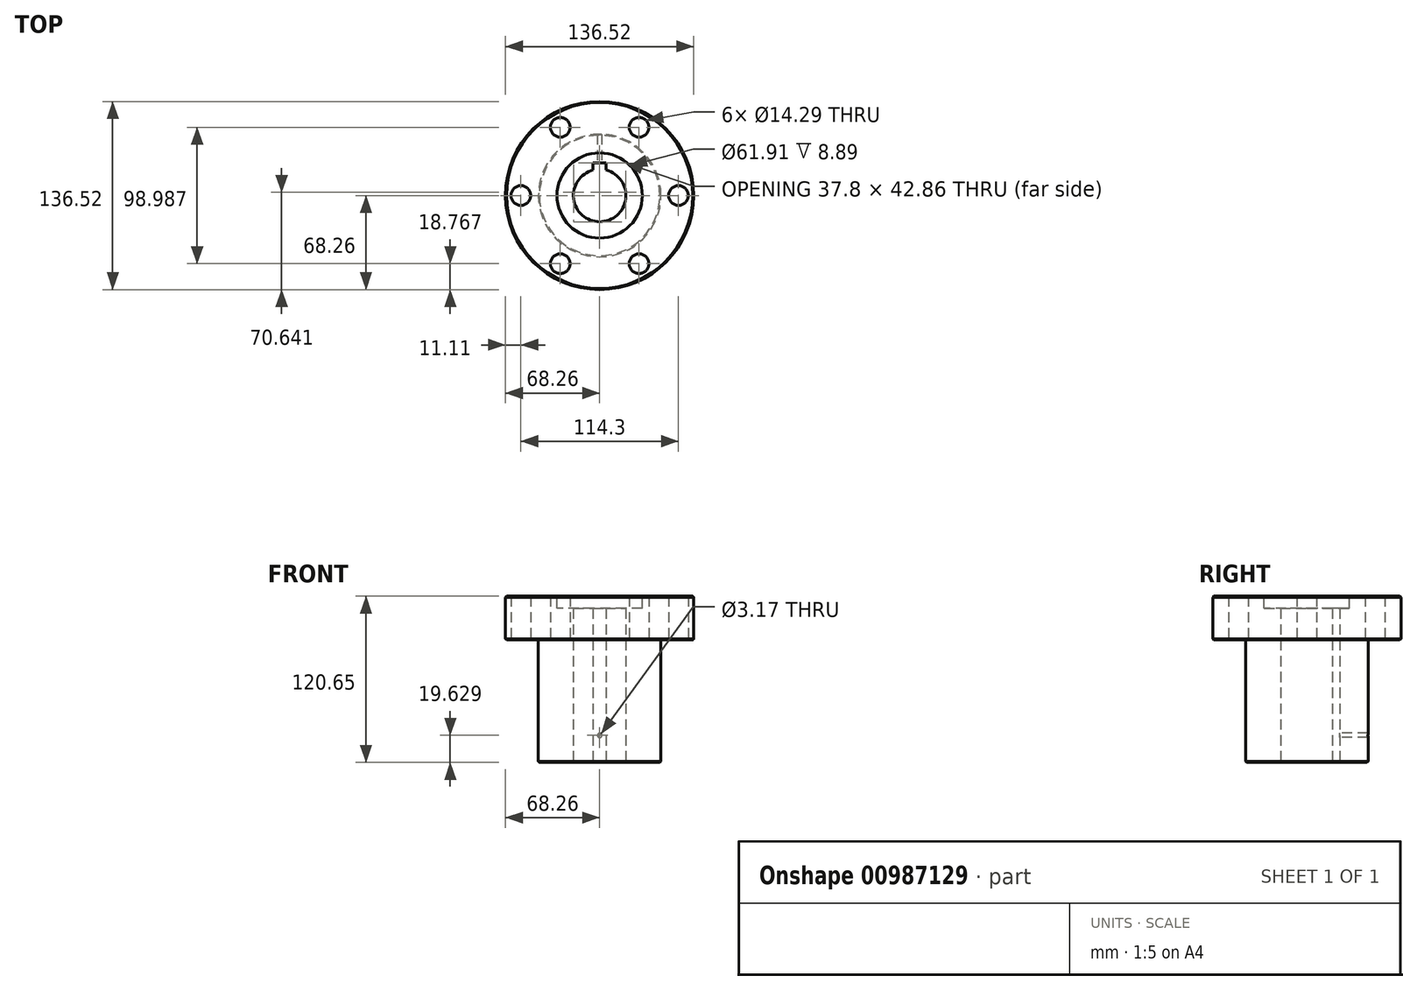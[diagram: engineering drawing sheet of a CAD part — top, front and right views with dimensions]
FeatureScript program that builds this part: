
annotation { "Feature Type Name" : "Feature", "Feature Type Description" : "" }
export const myFeature = defineFeature(function(context is Context, id is Id, definition is map)
    precondition{}
    {
        {
            var Q0;
            Q0=qCreatedBy(makeId("Top.planeOp"),FACE);
            var sketch = newSketch(context, id + "F0", { "sketchPlane" : qUnion([Q0])});
            skCircle(sketch, "E0", {"center": v(0, 0) * mm, "radius": 68.26 * mm});
            skCircle(sketch, "E1", {"center": v(0, 0) * mm, "radius": 19.05 * mm});
            skCircle(sketch, "E2", {"center": v(0, 0) * mm, "radius": 57.15 * mm, "construction": true});
            skLineSegment(sketch, "E3", {"start": v(0, 0) * mm, "end": v(0, 110.28) * mm, "construction": true});
            skLineSegment(sketch, "E4", {"start": v(0, 0) * mm, "end": v(56.56, 97.97) * mm, "construction": true});
            skCircle(sketch, "E5", {"center": v(28.58, 49.5) * mm, "radius": 7.14 * mm});
            skCircle(sketch, "E6.1.0", {"center": v(-28.57, 49.5) * mm, "radius": 7.14 * mm});
            skCircle(sketch, "E6.2.0", {"center": v(-57.15, 0) * mm, "radius": 7.14 * mm});
            skCircle(sketch, "E6.3.0", {"center": v(-28.58, -49.5) * mm, "radius": 7.14 * mm});
            skCircle(sketch, "E6.4.0", {"center": v(28.57, -49.5) * mm, "radius": 7.14 * mm});
            skCircle(sketch, "E6.5.0", {"center": v(57.15, 0) * mm, "radius": 7.14 * mm});
            skSolve(sketch);
        }
        {
            var Q0;
            Q0 = qSketchRegion(id + "F0", true);
            extrude(context, id + "F1", {"entities" : qUnion([Q0]), "depth" : 31.75 * mm, "offsetDistance" : 25.4 * mm});
        }
        {
            var Q0;
            Q0=makeQuery(id+"F1.opExtrude","CAP_FACE",FACE,{"disambiguationData":[OSD([sQuery(id+"F0.wireOp",EDGE,"E0"),sQuery(id+"F0.wireOp",EDGE,"E1"),sQuery(id+"F0.wireOp",EDGE,"E5"),sQuery(id+"F0.wireOp",EDGE,"E6.1.0"),sQuery(id+"F0.wireOp",EDGE,"E6.2.0"),sQuery(id+"F0.wireOp",EDGE,"E6.3.0"),sQuery(id+"F0.wireOp",EDGE,"E6.4.0"),sQuery(id+"F0.wireOp",EDGE,"E6.5.0")])],"isStart":false});
            var sketch = newSketch(context, id + "F2", { "sketchPlane" : qUnion([Q0])});
            skCircle(sketch, "E7", {"center": v(0, 0) * mm, "radius": 30.96 * mm});
            skSolve(sketch);
        }
        {
            var Q0;
            Q0 = qSketchRegion(id + "F2", true);
            extrude(context, id + "F3", {"entities" : qUnion([Q0]), "operationType" : NewBodyOperationType.REMOVE, "oppositeDirection" : true, "depth" : 8.9 * mm, "offsetDistance" : 25.4 * mm});
        }
        {
            var Q0;
            Q0=makeQuery(id+"F1.opExtrude","CAP_FACE",FACE,{"disambiguationData":[OSD([sQuery(id+"F0.wireOp",EDGE,"E0"),sQuery(id+"F0.wireOp",EDGE,"E1"),sQuery(id+"F0.wireOp",EDGE,"E5"),sQuery(id+"F0.wireOp",EDGE,"E6.1.0"),sQuery(id+"F0.wireOp",EDGE,"E6.2.0"),sQuery(id+"F0.wireOp",EDGE,"E6.3.0"),sQuery(id+"F0.wireOp",EDGE,"E6.4.0"),sQuery(id+"F0.wireOp",EDGE,"E6.5.0")])],"isStart":true});
            var sketch = newSketch(context, id + "F4", { "sketchPlane" : qUnion([Q0])});
            skCircle(sketch, "E8", {"center": v(0, 0) * mm, "radius": 44.45 * mm});
            skCircle(sketch, "E9", {"center": v(0, 0) * mm, "radius": 19.05 * mm});
            skSolve(sketch);
        }
        {
            var Q0;
            Q0 = qSketchRegion(id + "F4", true);
            extrude(context, id + "F5", {"entities" : qUnion([Q0]), "operationType" : NewBodyOperationType.ADD, "depth" : 88.9 * mm, "offsetDistance" : 25.4 * mm});
        }
        {
            var Q0;
            Q0=makeQuery(id+"F5.opExtrude","CAP_FACE",FACE,{"disambiguationData":[OSD([sQuery(id+"F4.wireOp",EDGE,"E8"),sQuery(id+"F4.wireOp",EDGE,"E9")])],"isStart":false});
            var sketch = newSketch(context, id + "F6", { "sketchPlane" : qUnion([Q0])});
            skLineSegment(sketch, "E10", {"start": v(0, 0) * mm, "end": v(0, -19.05) * mm});
            skLineSegment(sketch, "E11", {"start": v(0, -19.05) * mm, "end": v(0, -23.81) * mm});
            skLineSegment(sketch, "E12", {"start": v(0, -23.81) * mm, "end": v(-4.76, -23.81) * mm});
            skLineSegment(sketch, "E13", {"start": v(-4.76, -23.81) * mm, "end": v(-4.76, -10.52) * mm});
            skLineSegment(sketch, "E14", {"start": v(-4.76, -10.52) * mm, "end": v(4.76, -10.52) * mm});
            skLineSegment(sketch, "E15", {"start": v(4.76, -10.52) * mm, "end": v(4.76, -23.81) * mm});
            skLineSegment(sketch, "E16", {"start": v(4.76, -23.81) * mm, "end": v(0, -23.81) * mm});
            skSolve(sketch);
        }
        {
            var Q0;
            Q0 = qSketchRegion(id + "F6", true);
            extrude(context, id + "F7", {"entities" : qUnion([Q0]), "operationType" : NewBodyOperationType.REMOVE, "endBound" : BoundingType.THROUGH_ALL, "oppositeDirection" : true, "depth" : 25.4 * mm, "offsetDistance" : 25.4 * mm});
        }
        {
            var Q0;
            Q0=makeQuery(id+"F1.opExtrude","CAP_EDGE",EDGE,{"disambiguationData":[OSD([sQuery(id+"F0.wireOp",EDGE,"E0")])],"isStart":false});
            var Q1;
            Q1=makeQuery(id+"F1.opExtrude","CAP_EDGE",EDGE,{"disambiguationData":[OSD([sQuery(id+"F0.wireOp",EDGE,"E0")])],"isStart":true});
            var Q2;
            Q2=makeQuery(id+"F3.boolean.opBoolean","COPY",EDGE,{"derivedFrom":makeQuery(id+"F3.opExtrude","CAP_EDGE",EDGE,{"disambiguationData":[OSD([sQuery(id+"F2.wireOp",EDGE,"E7")])],"isStart":true})});
            var Q3;
            Q3=makeQuery(id+"F5.opExtrude","CAP_EDGE",EDGE,{"disambiguationData":[OSD([sQuery(id+"F4.wireOp",EDGE,"E8")])],"isStart":false});
            chamfer(context, id + "F8", {"entities" : qUnion([Q0, Q1, Q2, Q3]), "width" : 0.76 * mm, "tangentPropagation" : true});
        }
        {
            var Q0;
            Q0=qCreatedBy(makeId("Front.planeOp"),FACE);
            var sketch = newSketch(context, id + "F9", { "sketchPlane" : qUnion([Q0])});
            skCircle(sketch, "E17", {"center": v(0, -69.27) * mm, "radius": 1.59 * mm});
            skSolve(sketch);
        }
        {
            var Q0;
            Q0 = qSketchRegion(id + "F9", true);
            extrude(context, id + "F10", {"entities" : qUnion([Q0]), "operationType" : NewBodyOperationType.REMOVE, "oppositeDirection" : true, "depth" : 76.2 * mm, "offsetDistance" : 25.4 * mm});
        }
    });
